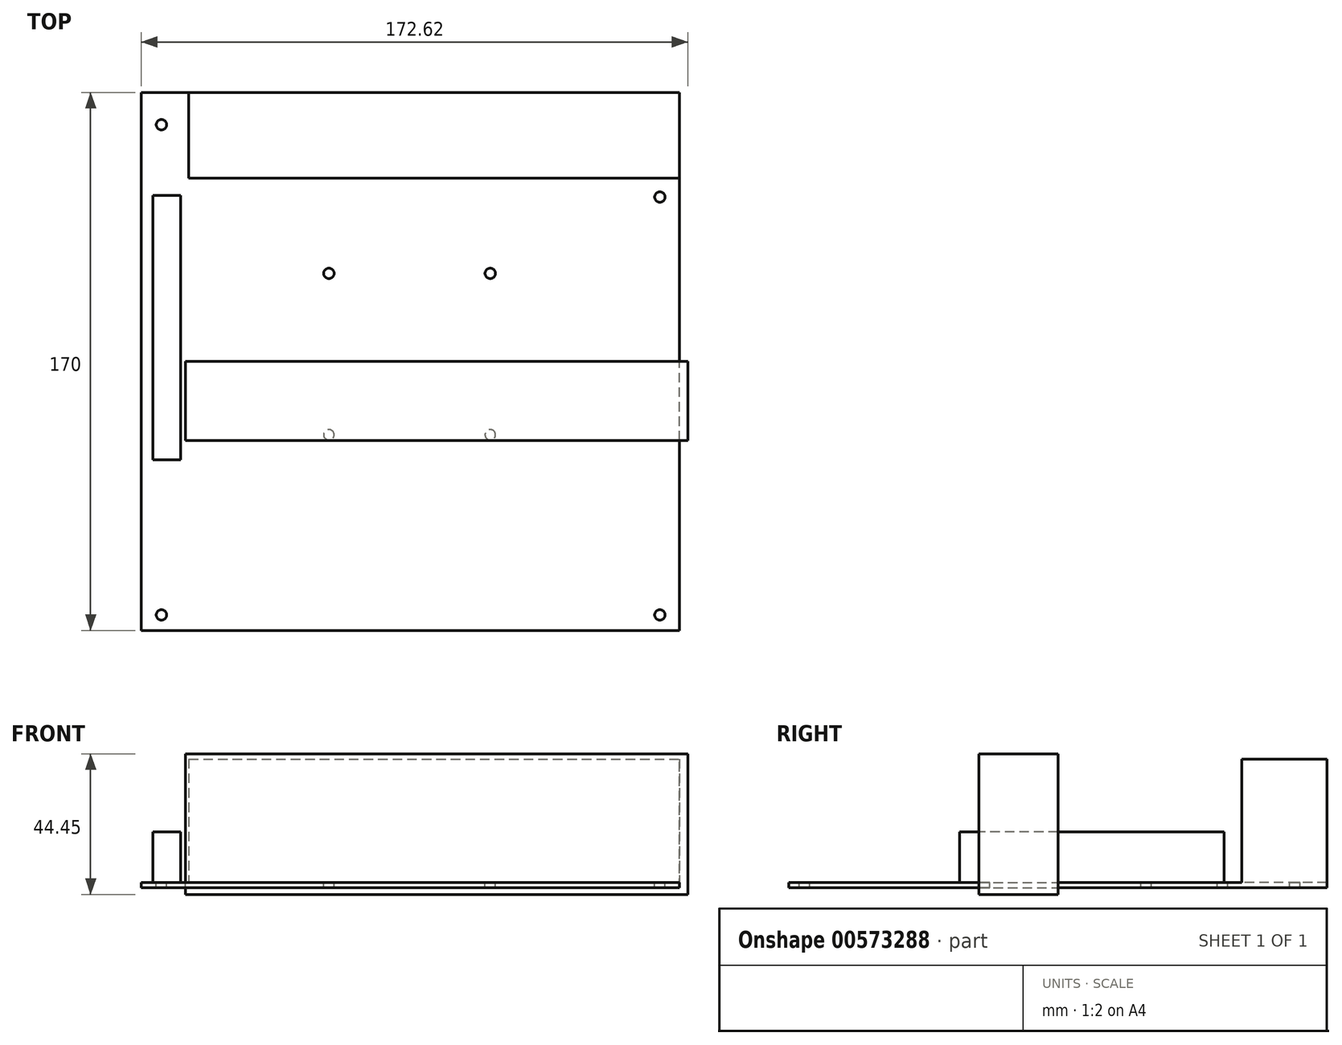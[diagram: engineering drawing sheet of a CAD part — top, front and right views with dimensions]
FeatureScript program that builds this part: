
annotation { "Feature Type Name" : "Feature", "Feature Type Description" : "" }
export const myFeature = defineFeature(function(context is Context, id is Id, definition is map)
    precondition{}
    {
        {
            var Q0;
            Q0=qCreatedBy(makeId("Top.planeOp"),FACE);
            var sketch = newSketch(context, id + "F0", { "sketchPlane" : qUnion([Q0])});
            skLineSegment(sketch, "E0.bottom", {"start": v(-85, -85) * mm, "end": v(85, -85) * mm});
            skLineSegment(sketch, "E0.top", {"start": v(-85, 85) * mm, "end": v(85, 85) * mm});
            skLineSegment(sketch, "E0.left", {"start": v(-85, -85) * mm, "end": v(-85, 85) * mm});
            skLineSegment(sketch, "E0.right", {"start": v(85, -85) * mm, "end": v(85, 85) * mm});
            skPoint(sketch, "E0.middle", {"position": v(0, 0) * mm});
            skPoint(sketch, "E1", {"position": v(-78.65, 74.84) * mm});
            skPoint(sketch, "E2", {"position": v(78.83, 51.98) * mm});
            skPoint(sketch, "E3", {"position": v(-78.65, -80.1) * mm});
            skPoint(sketch, "E4", {"position": v(78.83, -80.1) * mm});
            skLineSegment(sketch, "E5", {"start": v(-70, 85) * mm, "end": v(-70, -85) * mm});
            skLineSegment(sketch, "E6", {"start": v(-70, 58) * mm, "end": v(85, 58) * mm});
            skLineSegment(sketch, "E7", {"start": v(-70, -55) * mm, "end": v(85, -55) * mm});
            skSolve(sketch);
        }
        {
            var Q0;
            {var subQ5=sQuery(id+"F0.wireOp",EDGE,"E6");Q0=makeQuery(id+"F0.imprint","IMPRINT",FACE,{"disambiguationData":[TD([[makeQuery(id+"F0.imprint","IMPRINT",EDGE,{"derivedFrom":subQ5}),1.0]])]});}
            var Q1;
            {var subQ0=sQuery(id+"F0.wireOp",EDGE,"E6");Q1=makeQuery(id+"F0.imprint","IMPRINT",FACE,{"disambiguationData":[TD([[makeQuery(id+"F0.imprint","IMPRINT",EDGE,{"derivedFrom":subQ0}),-1.0]])]});}
            var Q2;
            {var subQ4=sQuery(id+"F0.wireOp",EDGE,"E0.left");Q2=makeQuery(id+"F0.imprint","IMPRINT",FACE,{"disambiguationData":[TD([[makeQuery(id+"F0.imprint","IMPRINT",EDGE,{"derivedFrom":subQ4}),-1.0]])]});}
            var Q3;
            {var subQ5=sQuery(id+"F0.wireOp",EDGE,"E7");Q3=makeQuery(id+"F0.imprint","IMPRINT",FACE,{"disambiguationData":[TD([[makeQuery(id+"F0.imprint","IMPRINT",EDGE,{"derivedFrom":subQ5}),-1.0]])]});}
            extrude(context, id + "F1", {"entities" : qUnion([Q0, Q1, Q2, Q3]), "oppositeDirection" : true, "depth" : 1.75 * mm, "offsetDistance" : 25 * mm});
        }
        {
            var Q0;
            {var subQ4=sQuery(id+"F0.wireOp",EDGE,"E0.left");Q0=makeQuery(id+"F0.imprint","IMPRINT",FACE,{"disambiguationData":[TD([[makeQuery(id+"F0.imprint","IMPRINT",EDGE,{"derivedFrom":subQ4}),-1.0]])]});}
            var sketch = newSketch(context, id + "F2", { "sketchPlane" : qUnion([Q0])});
            skLineSegment(sketch, "E8.bottom", {"start": v(-81.35, 52.52) * mm, "end": v(-72.65, 52.52) * mm});
            skLineSegment(sketch, "E8.top", {"start": v(-81.35, -31.06) * mm, "end": v(-72.65, -31.06) * mm});
            skLineSegment(sketch, "E8.left", {"start": v(-81.35, 52.52) * mm, "end": v(-81.35, -31.06) * mm});
            skLineSegment(sketch, "E8.right", {"start": v(-72.65, 52.52) * mm, "end": v(-72.65, -31.06) * mm});
            skPoint(sketch, "E9", {"position": v(-25.76, 27.83) * mm});
            skPoint(sketch, "E10", {"position": v(-25.76, -23.17) * mm});
            skPoint(sketch, "E11", {"position": v(25.24, -23.17) * mm});
            skPoint(sketch, "E12", {"position": v(25.24, 27.83) * mm});
            skPoint(sketch, "E13", {"position": v(-0.26, 2.33) * mm});
            skSolve(sketch);
        }
        {
            var Q0;
            Q0=makeQuery(id+"F2.imprint","IMPRINT",FACE,{"disambiguationData":[TD([[makeQuery(id+"F2.imprint","IMPRINT",EDGE,{"derivedFrom":sQuery(id+"F2.wireOp",EDGE,"E8.bottom")}),-1.0]])]});
            extrude(context, id + "F3", {"entities" : qUnion([Q0]), "operationType" : NewBodyOperationType.ADD, "depth" : 16 * mm, "offsetDistance" : 25 * mm});
        }
        {
            var Q0;
            Q0=qCreatedBy(makeId("Front.planeOp"),FACE);
            var sketch = newSketch(context, id + "F4", { "sketchPlane" : qUnion([Q0])});
            skLineSegment(sketch, "E14.bottom", {"start": v(87.62, -3.81) * mm, "end": v(-71.13, -3.81) * mm});
            skLineSegment(sketch, "E14.top", {"start": v(87.62, 40.64) * mm, "end": v(-71.13, 40.64) * mm});
            skLineSegment(sketch, "E14.left", {"start": v(87.62, -3.81) * mm, "end": v(87.62, 40.64) * mm});
            skLineSegment(sketch, "E14.right", {"start": v(-71.13, -3.81) * mm, "end": v(-71.13, 40.64) * mm});
            skSolve(sketch);
        }
        {
            var Q0;
            {var subQ5=sQuery(id+"F0.wireOp",EDGE,"E6");Q0=makeQuery(id+"F0.imprint","IMPRINT",FACE,{"disambiguationData":[TD([[makeQuery(id+"F0.imprint","IMPRINT",EDGE,{"derivedFrom":subQ5}),1.0]])]});}
            extrude(context, id + "F5", {"entities" : qUnion([Q0]), "operationType" : NewBodyOperationType.ADD, "depth" : 39 * mm, "offsetDistance" : 25 * mm});
        }
        {
            var Q0;
            Q0=sQuery(id+"F0.wireOp",VERTEX,"E3");
            var Q1;
            Q1=sQuery(id+"F0.wireOp",VERTEX,"E1");
            var Q2;
            Q2=sQuery(id+"F0.wireOp",VERTEX,"E4");
            var Q3;
            Q3=sQuery(id+"F0.wireOp",VERTEX,"E2");
            var Q4;
            Q4=sQuery(id+"F2.wireOp",VERTEX,"E10");
            var Q5;
            Q5=sQuery(id+"F2.wireOp",VERTEX,"E11");
            var Q6;
            Q6=sQuery(id+"F2.wireOp",VERTEX,"E12");
            var Q7;
            Q7=sQuery(id+"F2.wireOp",VERTEX,"E9");
            var Q8;
            Q8=makeQuery(id+"F1.opExtrude","SWEPT_BODY",BODY,{"disambiguationData":[OSD([sQuery(id+"F0.wireOp",EDGE,"E0.bottom"),sQuery(id+"F0.wireOp",EDGE,"E0.top"),sQuery(id+"F0.wireOp",EDGE,"E0.left"),sQuery(id+"F0.wireOp",EDGE,"E0.right")])]});
            hole(context, id + "F6", {"style" : HoleStyle.SIMPLE, "endStyle" : HoleEndStyle.THROUGH, "standardTappedOrClearance" : lookupTablePath({ "standard" : "ISO", "fit" : "Normal", "size" : "M3", "type" : "Clearance" }), "standardBlindInLast" : lookupTablePath({ "fit" : "Standard", "standard" : "ISO", "size" : "M3", "type" : "Clearance" }), "holeDiameter" : 3.3 * mm, "isTappedThrough" : true, "tappedDepth" : 12 * mm, "tapClearance" : 3, "locations" : qUnion([Q0, Q1, Q2, Q3, Q4, Q5, Q6, Q7]), "scope" : qUnion([Q8])});
        }
        {
            var Q0;
            Q0=makeQuery(id+"F4.imprint","IMPRINT",FACE,{"disambiguationData":[TD([[makeQuery(id+"F4.imprint","IMPRINT",EDGE,{"derivedFrom":sQuery(id+"F4.wireOp",EDGE,"E14.bottom")}),-1.0]])]});
            extrude(context, id + "F7", {"entities" : qUnion([Q0]), "depth" : 25 * mm, "offsetDistance" : 25 * mm});
        }
    });
